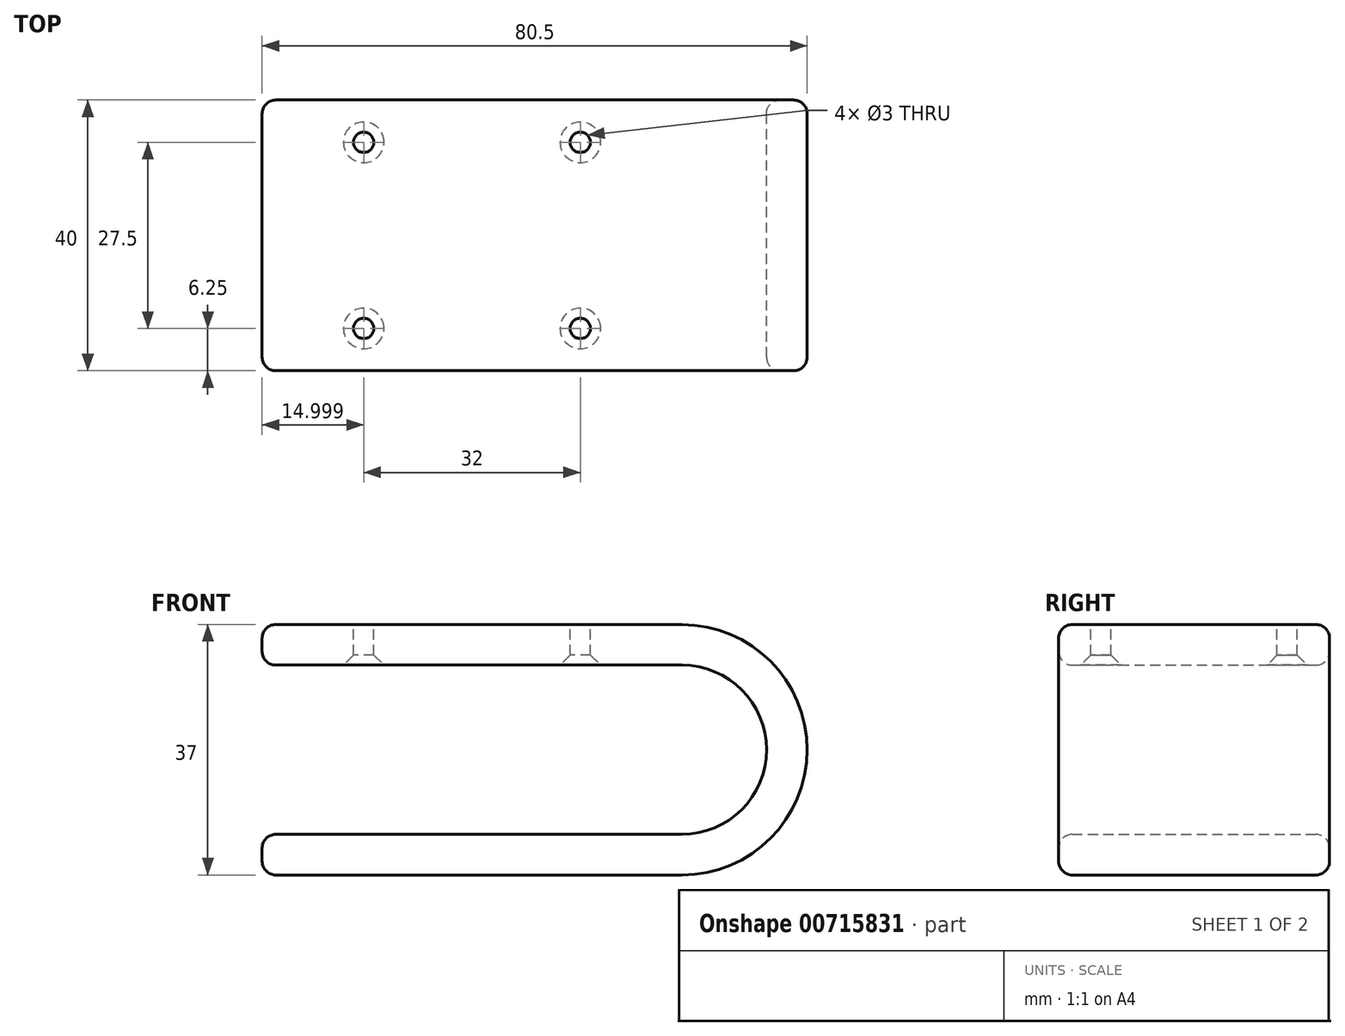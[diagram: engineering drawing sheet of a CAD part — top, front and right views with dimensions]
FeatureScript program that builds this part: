
annotation { "Feature Type Name" : "Feature", "Feature Type Description" : "" }
export const myFeature = defineFeature(function(context is Context, id is Id, definition is map)
    precondition{}
    {
        {
            var Q0;
            Q0=qCreatedBy(makeId("Front.planeOp"),FACE);
            var sketch = newSketch(context, id + "F0", { "sketchPlane" : qUnion([Q0])});
            skPoint(sketch, "E0.middle", {"position": v(0, 0) * mm});
            skPoint(sketch, "E1", {"position": v(-65.2, -2.45) * mm});
            skPoint(sketch, "E2", {"position": v(60.02, -2.45) * mm});
            skLineSegment(sketch, "E3", {"start": v(60.02, -2.45) * mm, "end": v(-65.2, -2.45) * mm});
            skLineSegment(sketch, "E4", {"start": v(-65.2, -2.45) * mm, "end": v(-65.2, 3.55) * mm});
            skPoint(sketch, "E5", {"position": v(62.8, 3.55) * mm});
            skLineSegment(sketch, "E6", {"start": v(62.8, 3.55) * mm, "end": v(-65.2, 3.55) * mm});
            skPoint(sketch, "E7", {"position": v(-65.2, -27.45) * mm});
            skLineSegment(sketch, "E8", {"start": v(-65.2, -27.45) * mm, "end": v(-3.2, -27.45) * mm});
            skLineSegment(sketch, "E9", {"start": v(-3.2, -27.45) * mm, "end": v(-3.2, -33.45) * mm});
            skLineSegment(sketch, "E10", {"start": v(-65.2, -27.45) * mm, "end": v(-65.2, -33.45) * mm});
            skLineSegment(sketch, "E11", {"start": v(-65.2, -33.45) * mm, "end": v(-3.2, -33.45) * mm});
            skPoint(sketch, "E12", {"position": v(-3.2, -2.45) * mm});
            skPoint(sketch, "E13", {"position": v(-3.2, 3.55) * mm});
            skLineSegment(sketch, "E14", {"start": v(-3.2, 3.55) * mm, "end": v(-3.2, -2.45) * mm});
            skPoint(sketch, "E15", {"position": v(-3.2, -14.95) * mm});
            skCircle(sketch, "E16", {"center": v(-3.2, -14.95) * mm, "radius": 12.5 * mm});
            skCircle(sketch, "E17", {"center": v(-3.2, -14.95) * mm, "radius": 18.5 * mm});
            skSolve(sketch);
        }
        {
            var Q0;
            {var subQ0=sQuery(id+"F0.wireOp",EDGE,"E4");Q0=makeQuery(id+"F0.imprint","IMPRINT",FACE,{"disambiguationData":[TD([[makeQuery(id+"F0.imprint","IMPRINT",EDGE,{"derivedFrom":subQ0}),-1.0]])]});}
            var Q1;
            {var subQ2=sQuery(id+"F0.wireOp",EDGE,"E3");var subQ5=sQuery(id+"F0.wireOp",EDGE,"PVoRK4Jb-RbM6-mkDD-Je3B-5WtLGLqPbE8g");var subQ7=makeQuery(id+"F0.imprint","INTERSECT",VERTEX,{"derivedFrom":[subQ2,subQ5]});Q1=makeQuery(id+"F0.imprint","IMPRINT",FACE,{"disambiguationData":[TD([[makeQuery(id+"F0.imprint","IMPRINT",EDGE,{"disambiguationData":[TD([[subQ7,-1.0]])],"derivedFrom":subQ2}),-1.0]])]});}
            var Q2;
            {var subQ0=sQuery(id+"F0.wireOp",EDGE,"ThXKMt8c-xMQV-VZvX-f5jr-xjYhEZgrqgih");Q2=makeQuery(id+"F0.imprint","IMPRINT",FACE,{"disambiguationData":[TD([[makeQuery(id+"F0.imprint","IMPRINT",EDGE,{"derivedFrom":subQ0}),1.0]])]});}
            var Q3;
            {var subQ0=sQuery(id+"F0.wireOp",EDGE,"E14");Q3=makeQuery(id+"F0.imprint","IMPRINT",FACE,{"disambiguationData":[TD([[makeQuery(id+"F0.imprint","IMPRINT",EDGE,{"derivedFrom":subQ0}),-1.0]])]});}
            var Q4;
            {var subQ5=sQuery(id+"F0.wireOp",EDGE,"E9");Q4=makeQuery(id+"F0.imprint","IMPRINT",FACE,{"disambiguationData":[TD([[makeQuery(id+"F0.imprint","IMPRINT",EDGE,{"derivedFrom":subQ5}),1.0]])]});}
            var Q5;
            {var subQ0=sQuery(id+"F0.wireOp",EDGE,"E9");Q5=makeQuery(id+"F0.imprint","IMPRINT",FACE,{"disambiguationData":[TD([[makeQuery(id+"F0.imprint","IMPRINT",EDGE,{"derivedFrom":subQ0}),-1.0]])]});}
            var Q6;
            {var subQ0=sQuery(id+"F0.wireOp",EDGE,"E10");Q6=makeQuery(id+"F0.imprint","IMPRINT",FACE,{"disambiguationData":[TD([[makeQuery(id+"F0.imprint","IMPRINT",EDGE,{"derivedFrom":subQ0}),1.0]])]});}
            extrude(context, id + "F1", {"entities" : qUnion([Q0, Q1, Q2, Q3, Q4, Q5, Q6]), "depth" : 40 * mm, "offsetDistance" : 25 * mm});
        }
        {
            var Q0;
            Q0=makeQuery(id+"F1.opExtrude","SWEPT_FACE",FACE,{"disambiguationData":[OSD([sQuery(id+"F0.wireOp",EDGE,"E3")])]});
            var sketch = newSketch(context, id + "F2", { "sketchPlane" : qUnion([Q0])});
            skPoint(sketch, "E18", {"position": v(-65.2, 20) * mm});
            skPoint(sketch, "E19", {"position": v(-42.2, 20) * mm});
            skPoint(sketch, "E20", {"position": v(-68.7, 20) * mm});
            skPoint(sketch, "E21", {"position": v(-42.2, 21.75) * mm});
            skPoint(sketch, "E22", {"position": v(-50.2, 40) * mm});
            skPoint(sketch, "E23", {"position": v(-50.2, 0) * mm});
            skPoint(sketch, "E24", {"position": v(-18.2, 40) * mm});
            skPoint(sketch, "E25", {"position": v(-18.2, 0) * mm});
            skPoint(sketch, "E26", {"position": v(-65.2, 33.75) * mm});
            skPoint(sketch, "E27", {"position": v(-65.2, 6.25) * mm});
            skPoint(sketch, "E28", {"position": v(-50.2, 6.25) * mm});
            skPoint(sketch, "E29", {"position": v(-50.2, 33.75) * mm});
            skPoint(sketch, "E30", {"position": v(-18.2, 33.75) * mm});
            skPoint(sketch, "E31", {"position": v(-18.2, 6.25) * mm});
            skSolve(sketch);
        }
        {
            var Q0;
            Q0=sQuery(id+"F2.wireOp",VERTEX,"E29");
            var Q1;
            Q1=sQuery(id+"F2.wireOp",VERTEX,"E28");
            var Q2;
            Q2=sQuery(id+"F2.wireOp",VERTEX,"E31");
            var Q3;
            Q3=sQuery(id+"F2.wireOp",VERTEX,"E30");
            var Q4;
            Q4=makeQuery(id+"F1.opExtrude","SWEPT_BODY",BODY,{"disambiguationData":[OSD([sQuery(id+"F0.wireOp",EDGE,"E0.top"),sQuery(id+"F0.wireOp",EDGE,"vq2HNmbg-jsjP-W6Yg-eore-kcwaKKdglXzY"),sQuery(id+"F0.wireOp",EDGE,"UBIgDiMd-d82X-4nfu-4dyT-G4HRnMGNyGZd"),sQuery(id+"F0.wireOp",EDGE,"E3"),sQuery(id+"F0.wireOp",EDGE,"E4"),sQuery(id+"F0.wireOp",EDGE,"JWN7pCiO-didE-iBMj-yQmq-FqHczA5lT94u"),sQuery(id+"F0.wireOp",EDGE,"OVg3XmLL-f2hG-dIpi-AOpd-NtP1ssGwRC9r"),sQuery(id+"F0.wireOp",EDGE,"3KNDwclB-sD22-SRQw-35Bx-RfWMGESJQFJb")])]});
            hole(context, id + "F3", {"style" : HoleStyle.C_SINK, "endStyle" : HoleEndStyle.BLIND, "holeDiameter" : 3 * mm, "cSinkDiameter" : 6 * mm, "cSinkAngle" : 90 * degree, "majorDiameter" : 5 * mm, "holeDepth" : 40 * mm, "isTappedThrough" : true, "tappedDepth" : 12 * mm, "tapClearance" : 3, "locations" : qUnion([Q0, Q1, Q2, Q3]), "scope" : qUnion([Q4])});
        }
        {
            var Q0;
            Q0=makeQuery(id+"F1.opExtrude","SWEPT_FACE",FACE,{"disambiguationData":[OSD([sQuery(id+"F0.wireOp",EDGE,"E4")])]});
            var Q1;
            Q1=makeQuery(id+"F1.opExtrude","CAP_FACE",FACE,{"disambiguationData":[OSD([sQuery(id+"F0.wireOp",EDGE,"E3"),sQuery(id+"F0.wireOp",EDGE,"E4"),sQuery(id+"F0.wireOp",EDGE,"E6"),sQuery(id+"F0.wireOp",EDGE,"E8"),sQuery(id+"F0.wireOp",EDGE,"E10"),sQuery(id+"F0.wireOp",EDGE,"E11"),sQuery(id+"F0.wireOp",EDGE,"E16"),sQuery(id+"F0.wireOp",EDGE,"E17")])],"isStart":true});
            var Q2;
            Q2=makeQuery(id+"F1.opExtrude","CAP_FACE",FACE,{"disambiguationData":[OSD([sQuery(id+"F0.wireOp",EDGE,"E3"),sQuery(id+"F0.wireOp",EDGE,"E4"),sQuery(id+"F0.wireOp",EDGE,"E6"),sQuery(id+"F0.wireOp",EDGE,"E8"),sQuery(id+"F0.wireOp",EDGE,"E10"),sQuery(id+"F0.wireOp",EDGE,"E11"),sQuery(id+"F0.wireOp",EDGE,"E16"),sQuery(id+"F0.wireOp",EDGE,"E17")])],"isStart":false});
            var Q3;
            Q3=makeQuery(id+"F1.opExtrude","SWEPT_EDGE",EDGE,{"disambiguationData":[OSD([sQuery(id+"F0.wireOp",EDGE,"E3"),sQuery(id+"F0.wireOp",EDGE,"E4")])]});
            var Q4;
            Q4=makeQuery(id+"F1.opExtrude","SWEPT_FACE",FACE,{"disambiguationData":[OSD([sQuery(id+"F0.wireOp",EDGE,"E10")])]});
            fillet(context, id + "F4", {"entities" : qUnion([Q0, Q1, Q2, Q3, Q4]), "radius" : 2 * mm, "tangentPropagation" : true, "allowEdgeOverflow" : false});
        }
    });
